# Revit family: Window-NanaWall-HSW-66_Swing_Slide
name_source: partatom
category: Windows
revit_build: Autodesk Revit Architecture 2013 (Build: 20130531_2115(x64)
units: mm (PartAtom-declared; Revit-internal decimal feet)

## types (1)
- Standard
    04 CSI = 08 41 13
    95 CSI = 8411
    Angle = 5.00°
    Assembly Code = B2030110
    Cost Info = http://www.nanawall.com
    Description = SwingSlide
    Engineering Details URL = http://www.nanawall.com
    Exterior Wall Offset = 0' - 0"
    Filler = <By Category>
    Glass Material = Glass - NanaWall - Generic
    Height = 12' - 0"
    Height Constraint = 9' - 6"
    Installation and Service URL = http://www.nanawall.com
    Manufacturer = NanaWall Systems, Inc.
    Manufacturer Fax = (415) 383-0312
    Max Panel Height = 9' - 1 65/128"
    Model = SwingSlide SwingSlide
    NanaWall Configurator = http://www.nanawall.com
    Opening Width = 10' - 11 253/256"
    Panel Height = 9' - 1 65/128"
    Performance URL = http://www.nanawall.com
    Product Page URL = http://www.nanawall.com
    Rough Height = 11' - 7 65/128"
    Rough Width = 11' - 6 7/64"
    Sash = Metal - NanaWall - Aluminum
    Subcategory = Folding Window
    Thickness = 0' - 2 5/8"
    URL = http://www.nanawall.com
    Wall Closure = By host
    Warranty URL = http://www.nanawall.com
    Width = 11' - 8"

## geometry (parser evidence)
native form markers: Blend x4, Sweep x23
no freeform markers — native parametric forms only
